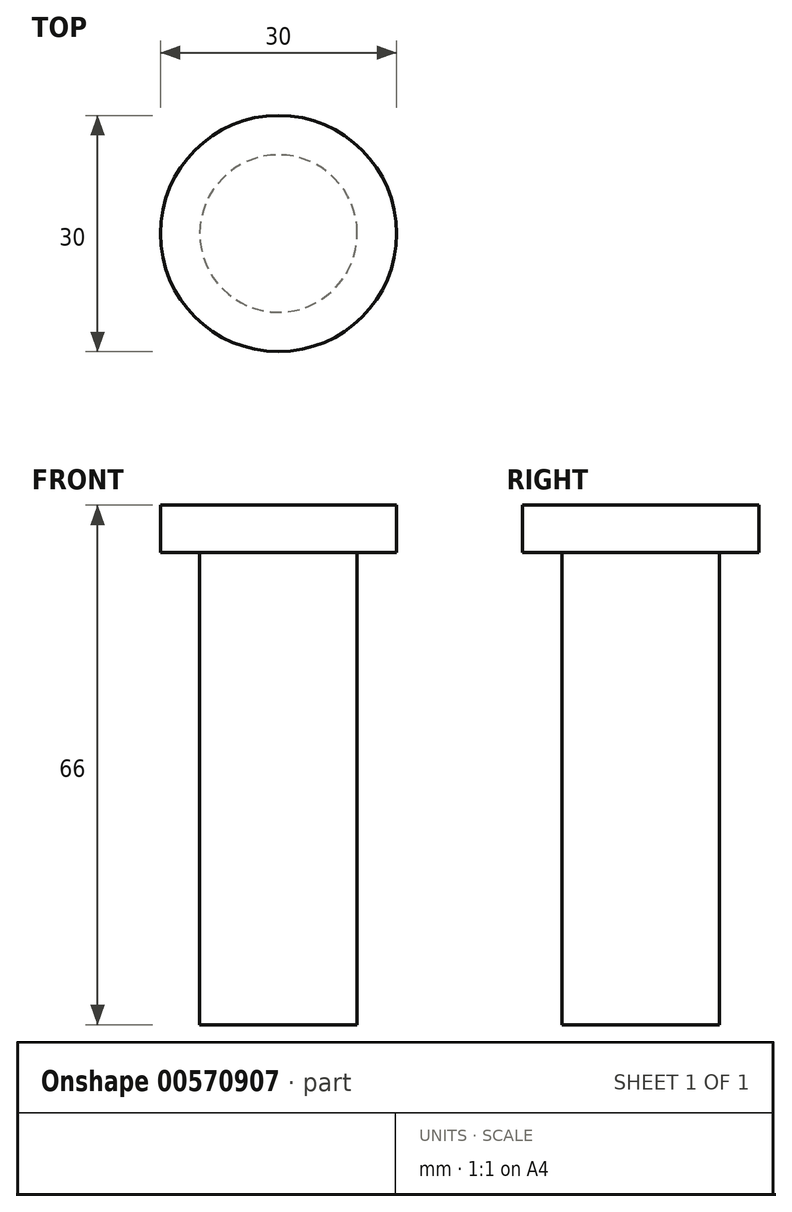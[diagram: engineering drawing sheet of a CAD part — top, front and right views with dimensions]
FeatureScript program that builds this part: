
annotation { "Feature Type Name" : "Feature", "Feature Type Description" : "" }
export const myFeature = defineFeature(function(context is Context, id is Id, definition is map)
    precondition{}
    {
        {
            var Q0;
            Q0=qCreatedBy(makeId("Top.planeOp"),FACE);
            var sketch = newSketch(context, id + "F0", { "sketchPlane" : qUnion([Q0])});
            skCircle(sketch, "E0", {"center": v(0, 0) * mm, "radius": 15 * mm});
            skSolve(sketch);
        }
        {
            var Q0;
            Q0 = qSketchRegion(id + "F0", true);
            extrude(context, id + "F1", {"entities" : qUnion([Q0]), "depth" : 6 * mm, "offsetDistance" : 25 * mm});
        }
        {
            var Q0;
            Q0=qCreatedBy(makeId("Top.planeOp"),FACE);
            var sketch = newSketch(context, id + "F2", { "sketchPlane" : qUnion([Q0])});
            skCircle(sketch, "E1", {"center": v(0, 0) * mm, "radius": 10 * mm});
            skSolve(sketch);
        }
        {
            var Q0;
            Q0 = qSketchRegion(id + "F2", true);
            extrude(context, id + "F3", {"entities" : qUnion([Q0]), "operationType" : NewBodyOperationType.ADD, "oppositeDirection" : true, "depth" : 60 * mm, "offsetDistance" : 25 * mm});
        }
    });
